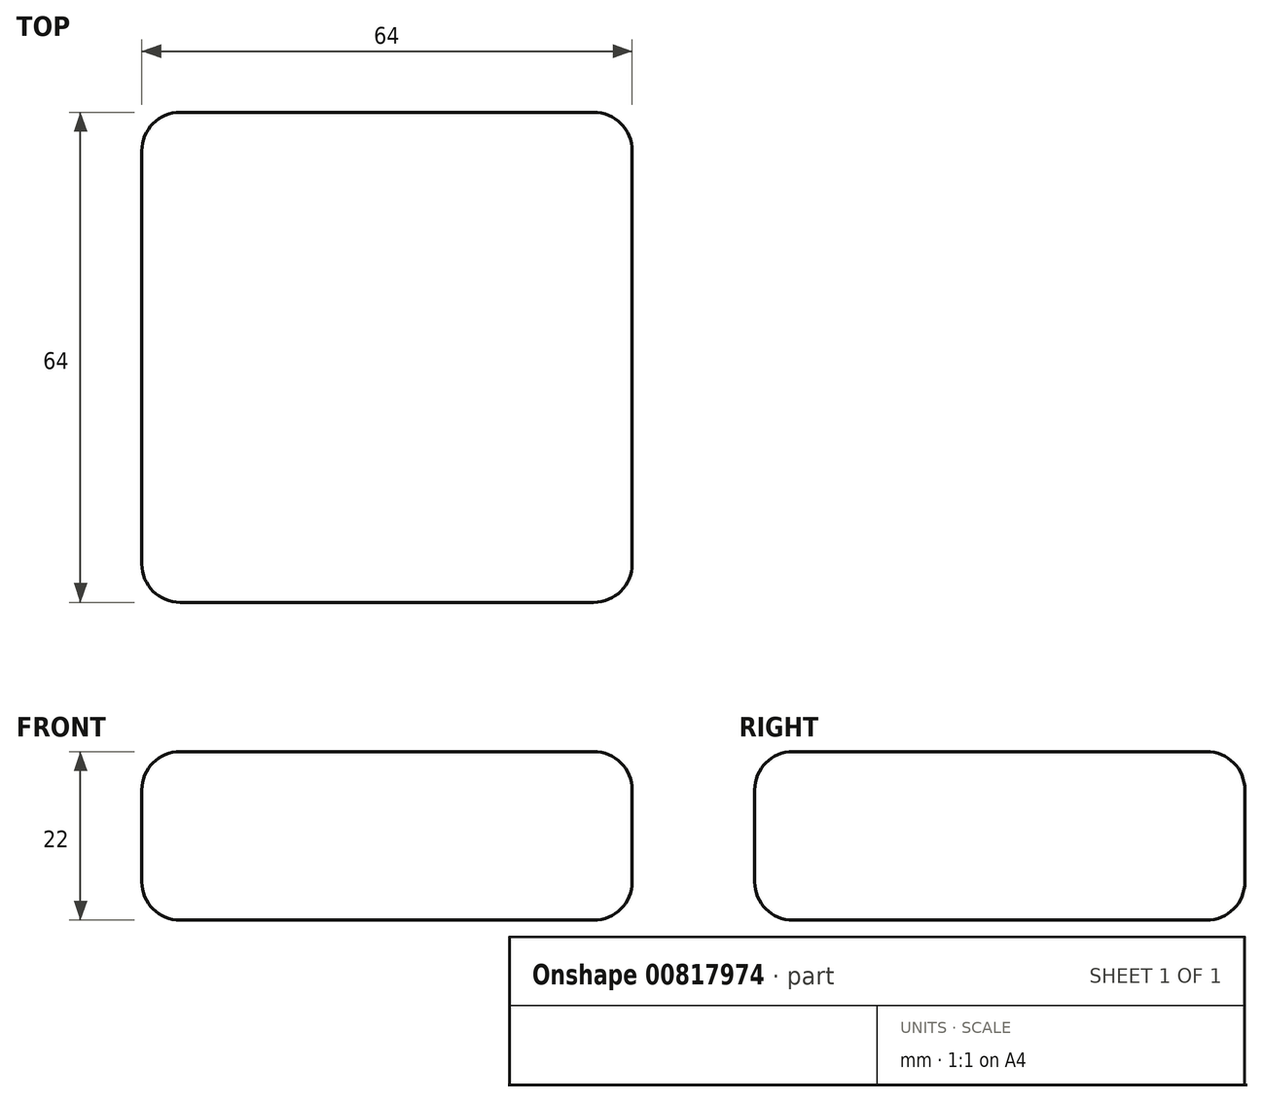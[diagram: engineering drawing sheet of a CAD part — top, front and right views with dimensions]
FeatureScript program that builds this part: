
annotation { "Feature Type Name" : "Feature", "Feature Type Description" : "" }
export const myFeature = defineFeature(function(context is Context, id is Id, definition is map)
    precondition{}
    {
        {
            var Q0;
            Q0=qCreatedBy(makeId("Top.planeOp"),FACE);
            var sketch = newSketch(context, id + "F0", { "sketchPlane" : qUnion([Q0])});
            skLineSegment(sketch, "E0.bottom", {"start": v(-32, -32) * mm, "end": v(32, -32) * mm});
            skLineSegment(sketch, "E0.top", {"start": v(-32, 32) * mm, "end": v(32, 32) * mm});
            skLineSegment(sketch, "E0.left", {"start": v(-32, -32) * mm, "end": v(-32, 32) * mm});
            skLineSegment(sketch, "E0.right", {"start": v(32, -32) * mm, "end": v(32, 32) * mm});
            skPoint(sketch, "E0.middle", {"position": v(0, 0) * mm});
            skSolve(sketch);
        }
        {
            var Q0;
            Q0=makeQuery(id+"F0.imprint","IMPRINT",FACE,{"disambiguationData":[TD([[makeQuery(id+"F0.imprint","IMPRINT",EDGE,{"derivedFrom":sQuery(id+"F0.wireOp",EDGE,"E0.bottom")}),1.0]])]});
            extrude(context, id + "F1", {"entities" : qUnion([Q0]), "depth" : 22 * mm, "offsetDistance" : 25 * mm});
        }
        {
            var Q0;
            Q0=makeQuery(id+"F1.opExtrude","CAP_EDGE",EDGE,{"disambiguationData":[OSD([sQuery(id+"F0.wireOp",EDGE,"E0.right")])],"isStart":false});
            var Q1;
            Q1=makeQuery(id+"F1.opExtrude","CAP_EDGE",EDGE,{"disambiguationData":[OSD([sQuery(id+"F0.wireOp",EDGE,"E0.bottom")])],"isStart":false});
            var Q2;
            Q2=makeQuery(id+"F1.opExtrude","CAP_EDGE",EDGE,{"disambiguationData":[OSD([sQuery(id+"F0.wireOp",EDGE,"E0.left")])],"isStart":false});
            var Q3;
            Q3=makeQuery(id+"F1.opExtrude","CAP_EDGE",EDGE,{"disambiguationData":[OSD([sQuery(id+"F0.wireOp",EDGE,"E0.top")])],"isStart":false});
            var Q4;
            Q4=makeQuery(id+"F1.opExtrude","SWEPT_EDGE",EDGE,{"disambiguationData":[OSD([sQuery(id+"F0.wireOp",EDGE,"E0.bottom"),sQuery(id+"F0.wireOp",EDGE,"E0.right")])]});
            var Q5;
            Q5=makeQuery(id+"F1.opExtrude","SWEPT_EDGE",EDGE,{"disambiguationData":[OSD([sQuery(id+"F0.wireOp",EDGE,"E0.top"),sQuery(id+"F0.wireOp",EDGE,"E0.right")])]});
            var Q6;
            Q6=makeQuery(id+"F1.opExtrude","SWEPT_EDGE",EDGE,{"disambiguationData":[OSD([sQuery(id+"F0.wireOp",EDGE,"E0.top"),sQuery(id+"F0.wireOp",EDGE,"E0.left")])]});
            var Q7;
            Q7=makeQuery(id+"F1.opExtrude","SWEPT_FACE",FACE,{"disambiguationData":[OSD([sQuery(id+"F0.wireOp",EDGE,"E0.left")])]});
            var Q8;
            Q8=makeQuery(id+"F1.opExtrude","CAP_EDGE",EDGE,{"disambiguationData":[OSD([sQuery(id+"F0.wireOp",EDGE,"E0.bottom")])],"isStart":true});
            var Q9;
            Q9=makeQuery(id+"F1.opExtrude","CAP_EDGE",EDGE,{"disambiguationData":[OSD([sQuery(id+"F0.wireOp",EDGE,"E0.top")])],"isStart":true});
            var Q10;
            Q10=makeQuery(id+"F1.opExtrude","CAP_EDGE",EDGE,{"disambiguationData":[OSD([sQuery(id+"F0.wireOp",EDGE,"E0.right")])],"isStart":true});
            fillet(context, id + "F2", {"entities" : qUnion([Q0, Q1, Q2, Q3, Q4, Q5, Q6, Q7, Q8, Q9, Q10]), "radius" : 5 * mm, "tangentPropagation" : true, "allowEdgeOverflow" : false});
        }
    });
